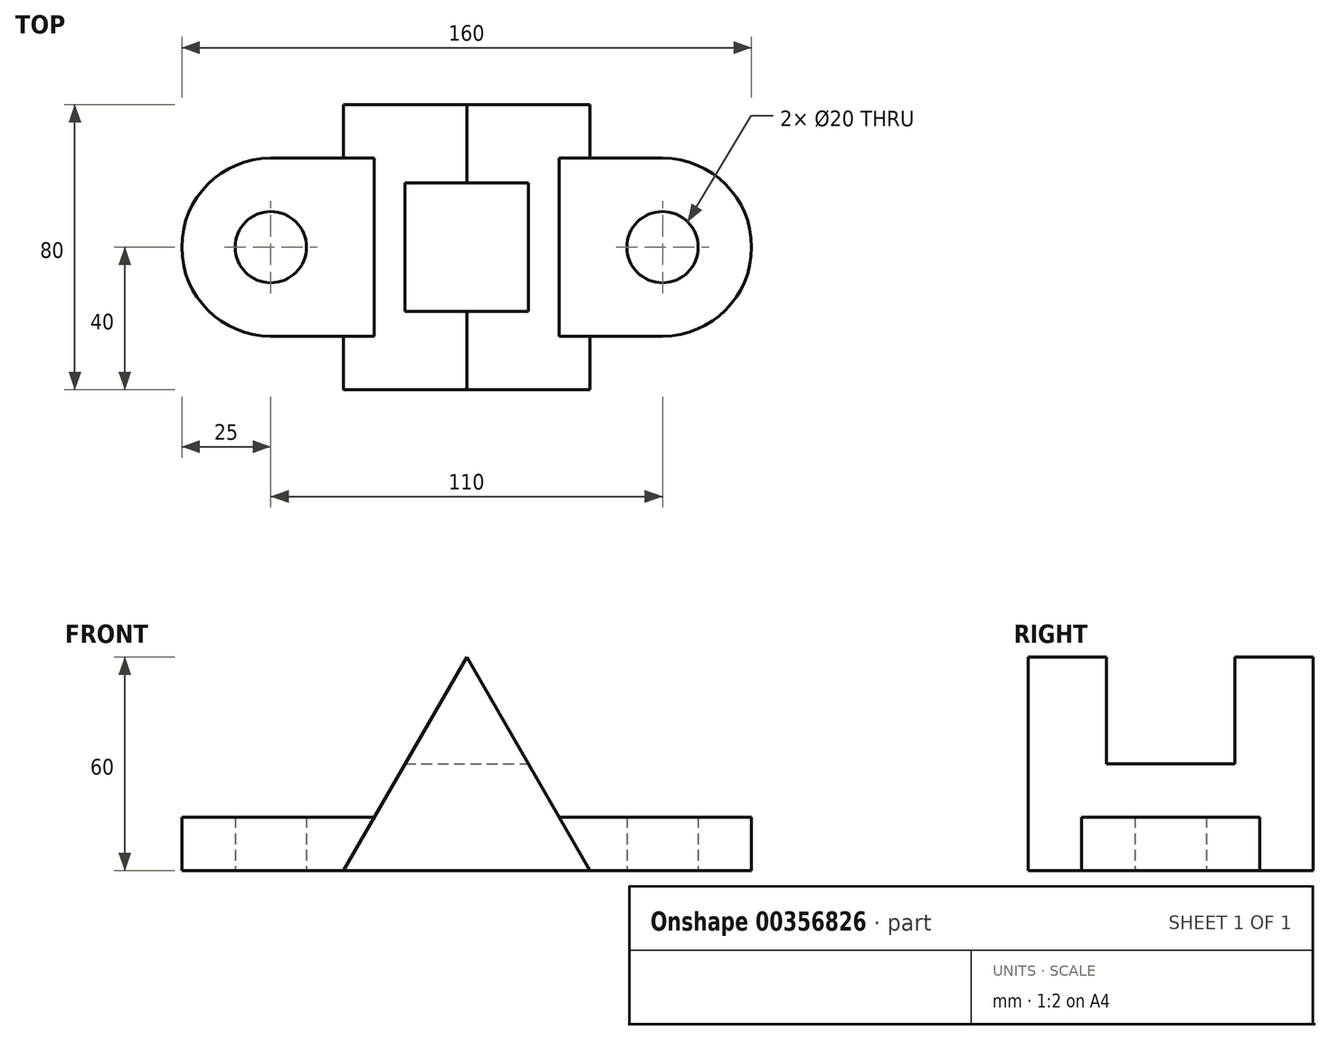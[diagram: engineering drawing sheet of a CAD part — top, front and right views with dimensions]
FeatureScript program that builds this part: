
annotation { "Feature Type Name" : "Feature", "Feature Type Description" : "" }
export const myFeature = defineFeature(function(context is Context, id is Id, definition is map)
    precondition{}
    {
        {
            var Q0;
            Q0=qCreatedBy(makeId("Top.planeOp"),FACE);
            var sketch = newSketch(context, id + "F0", { "sketchPlane" : qUnion([Q0])});
            skCircle(sketch, "E0", {"center": v(0, 0) * mm, "radius": 10 * mm});
            skArc(sketch, "E1", {"start": v(0, -25) * mm, "mid": v(25, 0) * mm, "end": v(0, 25) * mm});
            skLineSegment(sketch, "E2", {"start": v(-55, 25) * mm, "end": v(-55, 27.54) * mm, "construction": true});
            skPoint(sketch, "E3.endSnap0", {"position": v(-55, 13.77) * mm});
            skArc(sketch, "E4.MirrorC", {"start": v(-110, -25) * mm, "mid": v(-135, 0) * mm, "end": v(-110, 25) * mm});
            skCircle(sketch, "E5.MirrorC", {"center": v(-110, 0) * mm, "radius": 10 * mm});
            skLineSegment(sketch, "E6", {"start": v(-110, 25) * mm, "end": v(0, 25) * mm});
            skLineSegment(sketch, "E7.MirrorCS", {"start": v(-110, -25) * mm, "end": v(0, -25) * mm});
            skPoint(sketch, "E8.orphan", {"position": v(-55, 43.45) * mm});
            skPoint(sketch, "E9.MirrorCS.start.orphan", {"position": v(-55, 0) * mm});
            skSolve(sketch);
        }
        {
            var Q0;
            Q0=makeQuery(id+"F0.imprint","IMPRINT",FACE,{"disambiguationData":[TD([[makeQuery(id+"F0.imprint","IMPRINT",EDGE,{"derivedFrom":sQuery(id+"F0.wireOp",EDGE,"E0")}),-1.0]])]});
            extrude(context, id + "F1", {"entities" : qUnion([Q0]), "depth" : 15 * mm});
        }
        {
            var Q0;
            Q0=qCreatedBy(makeId("Front.planeOp"),FACE);
            var sketch = newSketch(context, id + "F2", { "sketchPlane" : qUnion([Q0])});
            skLineSegment(sketch, "E10", {"start": v(-20.36, 0) * mm, "end": v(-55, 0) * mm});
            skLineSegment(sketch, "E11", {"start": v(-55, 0) * mm, "end": v(-55, 60) * mm});
            skLineSegment(sketch, "E12", {"start": v(-55, 60) * mm, "end": v(-20.36, 0) * mm});
            skLineSegment(sketch, "E13.MirrorCS", {"start": v(-55, 60) * mm, "end": v(-89.64, 0) * mm});
            skLineSegment(sketch, "E14", {"start": v(-89.64, 0) * mm, "end": v(-55, 0) * mm});
            skSolve(sketch);
        }
        {
            var Q0;
            Q0=makeQuery(id+"F2.imprint","IMPRINT",FACE,{"disambiguationData":[TD([[makeQuery(id+"F2.imprint","IMPRINT",EDGE,{"derivedFrom":sQuery(id+"F2.wireOp",EDGE,"E11")}),1.0]])]});
            var Q1;
            Q1=makeQuery(id+"F2.imprint","IMPRINT",FACE,{"disambiguationData":[TD([[makeQuery(id+"F2.imprint","IMPRINT",EDGE,{"derivedFrom":sQuery(id+"F2.wireOp",EDGE,"E10")}),-1.0]])]});
            extrude(context, id + "F3", {"entities" : qUnion([Q0, Q1]), "operationType" : NewBodyOperationType.ADD, "depth" : 40 * mm});
        }
        {
            var Q0;
            Q0=makeQuery(id+"F3.opExtrude","CAP_FACE",FACE,{"disambiguationData":[OSD([sQuery(id+"F2.wireOp",EDGE,"E10"),sQuery(id+"F2.wireOp",EDGE,"E12"),sQuery(id+"F2.wireOp",EDGE,"E13.MirrorCS"),sQuery(id+"F2.wireOp",EDGE,"E14")])],"isStart":false});
            extrude(context, id + "F4", {"entities" : qUnion([Q0]), "operationType" : NewBodyOperationType.ADD, "depth" : -80 * mm});
        }
        {
            var Q0;
            Q0=qCreatedBy(makeId("Right.planeOp"),FACE);
            var sketch = newSketch(context, id + "F5", { "sketchPlane" : qUnion([Q0])});
            skLineSegment(sketch, "E15.bottom", {"start": v(-18, 60) * mm, "end": v(18, 60) * mm});
            skLineSegment(sketch, "E15.top", {"start": v(-18, 30) * mm, "end": v(18, 30) * mm});
            skLineSegment(sketch, "E15.left", {"start": v(-18, 60) * mm, "end": v(-18, 30) * mm});
            skLineSegment(sketch, "E15.right", {"start": v(18, 60) * mm, "end": v(18, 30) * mm});
            skSolve(sketch);
        }
        {
            var Q0;
            Q0=makeQuery(id+"F5.imprint","IMPRINT",FACE,{"disambiguationData":[TD([[makeQuery(id+"F5.imprint","IMPRINT",EDGE,{"derivedFrom":sQuery(id+"F5.wireOp",EDGE,"E15.bottom")}),-1.0]])]});
            extrude(context, id + "F6", {"entities" : qUnion([Q0]), "operationType" : NewBodyOperationType.REMOVE, "oppositeDirection" : true, "depth" : 80 * mm});
        }
    });
